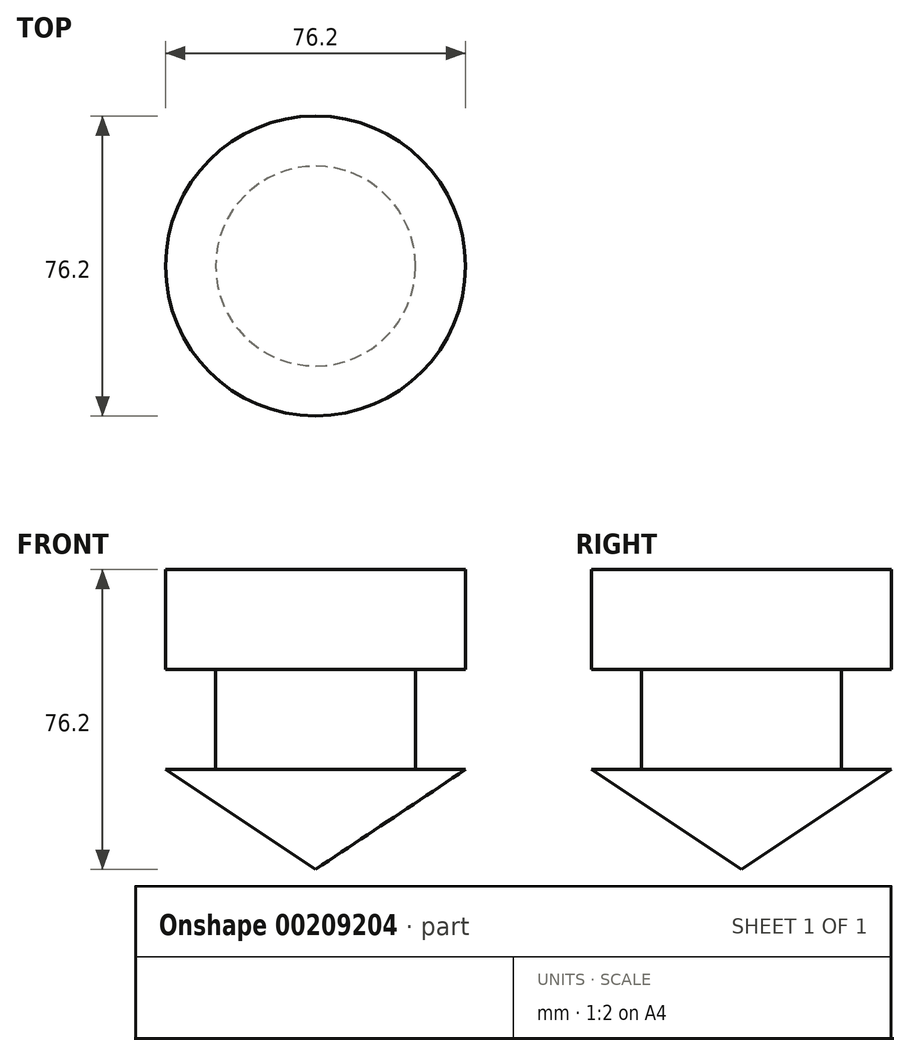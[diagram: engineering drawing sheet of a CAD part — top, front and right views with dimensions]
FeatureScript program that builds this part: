
annotation { "Feature Type Name" : "Feature", "Feature Type Description" : "" }
export const myFeature = defineFeature(function(context is Context, id is Id, definition is map)
    precondition{}
    {
        {
            var Q0;
            Q0=qCreatedBy(makeId("Front.planeOp"),FACE);
            var sketch = newSketch(context, id + "F0", { "sketchPlane" : qUnion([Q0])});
            skLineSegment(sketch, "E0", {"start": v(0, 0) * mm, "end": v(0, 76.2) * mm});
            skLineSegment(sketch, "E1", {"start": v(0, 76.2) * mm, "end": v(38.1, 76.2) * mm});
            skLineSegment(sketch, "E2", {"start": v(38.1, 76.2) * mm, "end": v(38.1, 50.8) * mm});
            skLineSegment(sketch, "E3", {"start": v(38.1, 50.8) * mm, "end": v(25.4, 50.8) * mm});
            skLineSegment(sketch, "E4", {"start": v(25.4, 50.8) * mm, "end": v(25.4, 25.4) * mm});
            skLineSegment(sketch, "E5", {"start": v(25.4, 25.4) * mm, "end": v(38.1, 25.4) * mm});
            skLineSegment(sketch, "E6", {"start": v(38.1, 25.4) * mm, "end": v(0, 0) * mm});
            skSolve(sketch);
        }
        {
            var Q0;
            Q0=makeQuery(id+"F0.imprint","IMPRINT",FACE,{"disambiguationData":[TD([[makeQuery(id+"F0.imprint","IMPRINT",EDGE,{"derivedFrom":sQuery(id+"F0.wireOp",EDGE,"E0")}),-1.0]])]});
            var Q1;
            Q1=sQuery(id+"F0.wireOp",EDGE,"E0");
            revolve(context, id + "F1", {"entities" : qUnion([Q0]), "axis" : qUnion([Q1]), "revolveType" : RevolveType.FULL});
        }
    });
